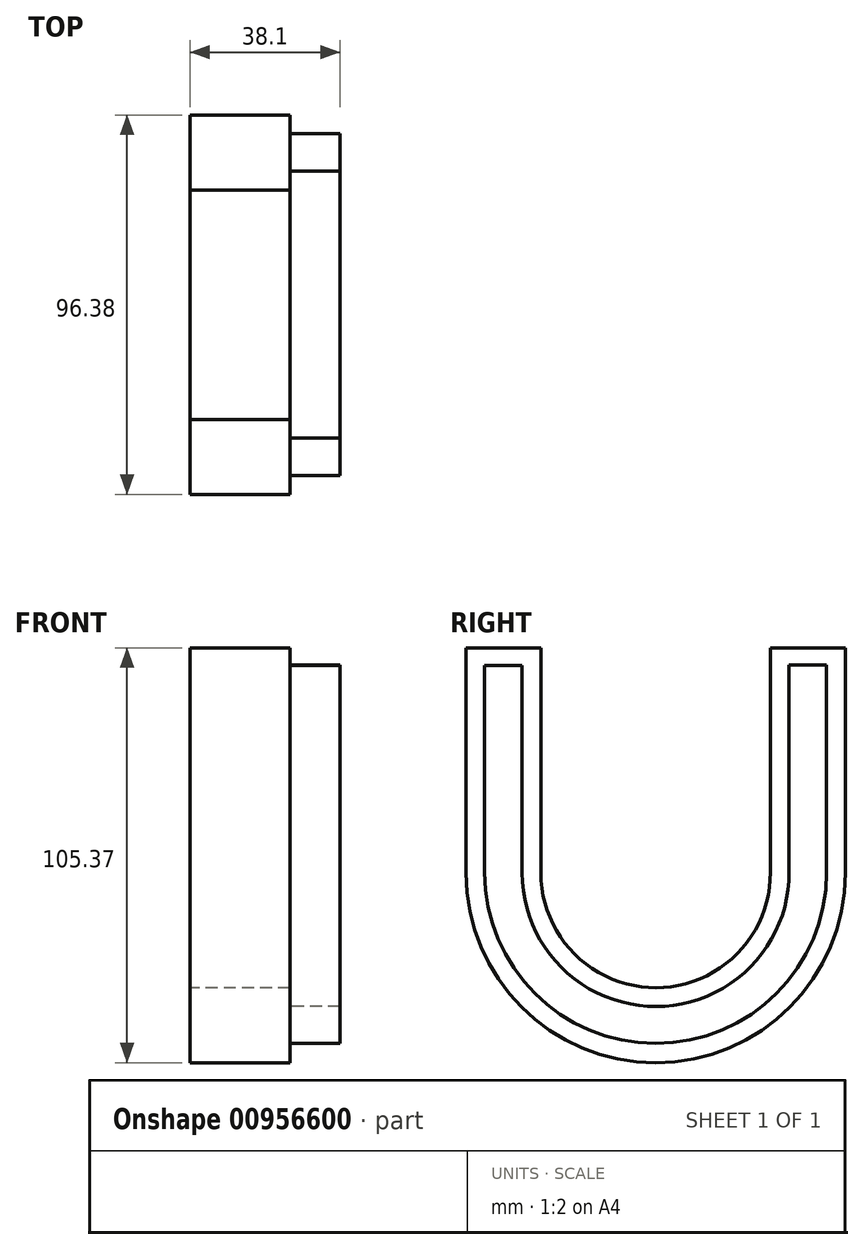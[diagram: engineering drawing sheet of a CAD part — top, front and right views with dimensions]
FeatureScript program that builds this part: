
annotation { "Feature Type Name" : "Feature", "Feature Type Description" : "" }
export const myFeature = defineFeature(function(context is Context, id is Id, definition is map)
    precondition{}
    {
        {
            var Q0;
            Q0=qCreatedBy(makeId("Right.planeOp"),FACE);
            var sketch = newSketch(context, id + "F0", { "sketchPlane" : qUnion([Q0])});
            skLineSegment(sketch, "E0", {"start": v(-47.36, 76.14) * mm, "end": v(-47.36, 18.99) * mm});
            skLineSegment(sketch, "E1", {"start": v(49.02, 76.14) * mm, "end": v(49.02, 18.99) * mm});
            skArc(sketch, "E2", {"start": v(-47.36, 18.99) * mm, "mid": v(0.83, -29.2) * mm, "end": v(49.02, 18.99) * mm});
            skLineSegment(sketch, "E3", {"start": v(-47.36, 76.14) * mm, "end": v(-28.31, 76.14) * mm});
            skLineSegment(sketch, "E4", {"start": v(29.97, 76.17) * mm, "end": v(49.02, 76.14) * mm});
            skLineSegment(sketch, "E5", {"start": v(-28.31, 76.14) * mm, "end": v(-28.31, 18.99) * mm});
            skLineSegment(sketch, "E6", {"start": v(29.97, 76.34) * mm, "end": v(29.97, 19.2) * mm});
            skArc(sketch, "E7", {"start": v(-28.31, 18.99) * mm, "mid": v(0.93, -10.15) * mm, "end": v(29.97, 19.2) * mm});
            skSolve(sketch);
        }
        {
            var Q0;
            Q0=makeQuery(id+"F0.imprint","IMPRINT",FACE,{"disambiguationData":[TD([[makeQuery(id+"F0.imprint","IMPRINT",EDGE,{"derivedFrom":sQuery(id+"F0.wireOp",EDGE,"E0")}),1.0]])]});
            extrude(context, id + "F1", {"entities" : qUnion([Q0]), "depth" : 25.4 * mm, "offsetDistance" : 25.4 * mm});
        }
        {
            var Q0;
            Q0=makeQuery(id+"F1.opExtrude","CAP_FACE",FACE,{"disambiguationData":[OSD([sQuery(id+"F0.wireOp",EDGE,"E0"),sQuery(id+"F0.wireOp",EDGE,"E1"),sQuery(id+"F0.wireOp",EDGE,"E2"),sQuery(id+"F0.wireOp",EDGE,"E3"),sQuery(id+"F0.wireOp",EDGE,"E4"),sQuery(id+"F0.wireOp",EDGE,"E5"),sQuery(id+"F0.wireOp",EDGE,"E6"),sQuery(id+"F0.wireOp",EDGE,"E7")])],"isStart":false});
            var sketch = newSketch(context, id + "F2", { "sketchPlane" : qUnion([Q0])});
            skLineSegment(sketch, "E8", {"start": v(-42.6, 71.7) * mm, "end": v(-33.07, 71.7) * mm});
            skLineSegment(sketch, "E9", {"start": v(-33.07, 71.7) * mm, "end": v(-33.07, 18.99) * mm});
            skLineSegment(sketch, "E10", {"start": v(-42.6, 71.7) * mm, "end": v(-42.6, 19.12) * mm});
            skLineSegment(sketch, "E11", {"start": v(34.74, 71.8) * mm, "end": v(44.26, 71.8) * mm});
            skLineSegment(sketch, "E12", {"start": v(44.26, 71.8) * mm, "end": v(44.26, 19.12) * mm});
            skLineSegment(sketch, "E13", {"start": v(34.74, 71.8) * mm, "end": v(34.74, 19.2) * mm});
            skArc(sketch, "E14", {"start": v(-42.6, 19.12) * mm, "mid": v(0.83, -24.31) * mm, "end": v(44.26, 19.12) * mm});
            skArc(sketch, "E15", {"start": v(-33.07, 18.99) * mm, "mid": v(0.93, -14.92) * mm, "end": v(34.74, 19.2) * mm});
            skSolve(sketch);
        }
        {
            var Q0;
            Q0=makeQuery(id+"F2.imprint","IMPRINT",FACE,{"disambiguationData":[TD([[makeQuery(id+"F2.imprint","IMPRINT",EDGE,{"derivedFrom":sQuery(id+"F2.wireOp",EDGE,"E8")}),-1.0]])]});
            extrude(context, id + "F3", {"entities" : qUnion([Q0]), "depth" : 12.7 * mm, "offsetDistance" : 25.4 * mm});
        }
    });
